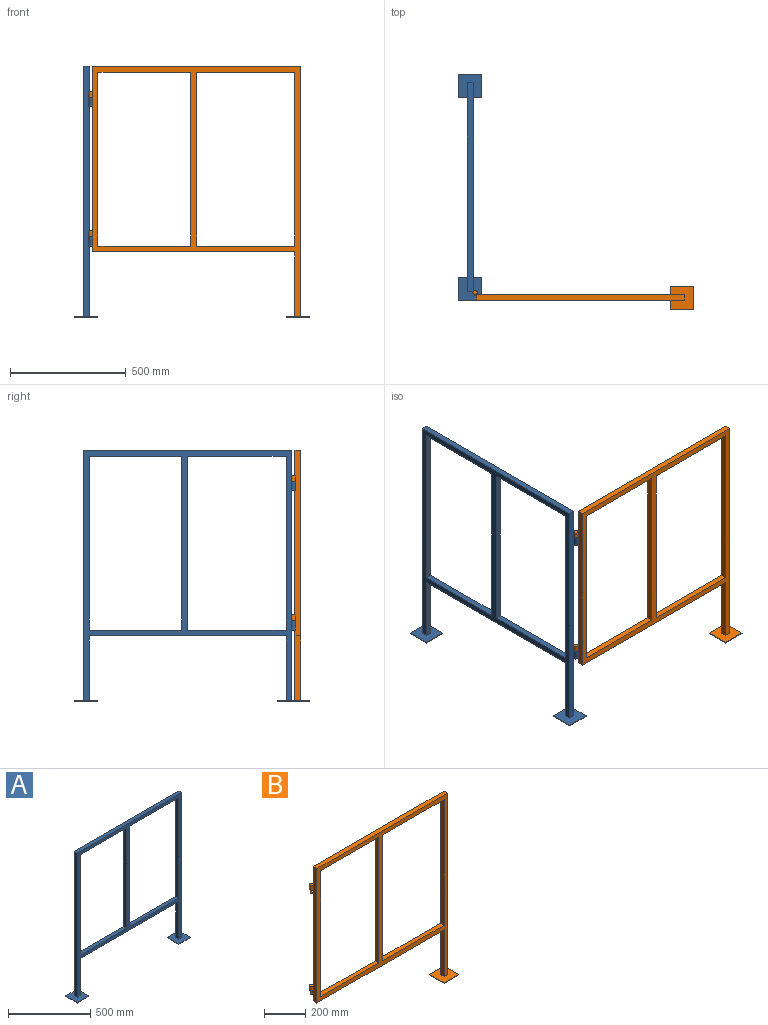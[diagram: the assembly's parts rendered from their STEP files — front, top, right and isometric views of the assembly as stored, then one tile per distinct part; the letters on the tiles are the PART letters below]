
ASSEMBLY  parts=2 mates=1
PART A: 38 faces, bbox 974.6x100x1083 mm
  f0: plane 1080x25.4mm, normal (-1,0,0), area 27432mm2, adj f13,f14,f15,f16
  f1: plane 280x25.4mm, normal (1,0,0), area 7112mm2, adj f2,f14,f15,f16
  f2: plane 849.2x25.4mm, normal (0,0,-1), area 21569.7mm2, adj f1,f3,f14,f15
  f3: plane 280x25.4mm, normal (-1,0,0), area 7112mm2, adj f2,f14,f15,f22
  f4: plane 1080x25.4mm, normal (1,0,0), area 27361.7mm2, adj f13,f14,f15,f22,f28,f29,f30,f33
  f5: plane 749.2x25.4mm, normal (1,0,0), area 19029.7mm2, adj f6,f11,f14,f15
  f6: plane 423.8x25.4mm, normal (0,0,-1), area 10764.5mm2, adj f5,f7,f14,f15
  f7: plane 749.2x25.4mm, normal (-1,0,0), area 19029.7mm2, adj f6,f11,f14,f15
  f8: plane 749.2x25.4mm, normal (1,0,0), area 19029.7mm2, adj f9,f12,f14,f15
  f9: plane 400x25.4mm, normal (0,0,-1), area 10160mm2, adj f8,f10,f14,f15
  f10: plane 749.2x25.4mm, normal (-1,0,0), area 19029.7mm2, adj f9,f12,f14,f15
  f11: plane 423.8x25.4mm, normal (0,0,1), area 10764.5mm2, adj f5,f7,f14,f15
  f12: plane 400x25.4mm, normal (0,0,1), area 10160mm2, adj f8,f10,f14,f15
  f13: plane 900x25.4mm, normal (0,0,1), area 22860mm2, adj f0,f4,f14,f15
  f14: plane 1080x900mm, normal (0,1,0), area 116921mm2, adj f0,f1,f2,f3,f4,f5,f6,f7
  f15: plane 1080x900mm, normal (0,-1,0), area 117033mm2, adj f0,f1,f2,f3,f4,f5,f6,f7
  f16: plane 100x100mm, normal (0,0,1), area 9354.8mm2, adj f0,f1,f14,f15,f17,f18,f19,f20
  f17: plane 100x3mm, normal (0,-1,0), area 300mm2, adj f16,f18,f20,f21
  f18: plane 100x3mm, normal (-1,0,0), area 300mm2, adj f16,f17,f19,f21
  f19: plane 100x3mm, normal (0,1,0), area 300mm2, adj f16,f18,f20,f21
  f20: plane 100x3mm, normal (1,0,0), area 300mm2, adj f16,f17,f19,f21
  f21: plane 100x100mm, normal (0,0,-1), area 10000mm2, adj f17,f18,f19,f20
  f22: plane 100x100mm, normal (0,0,1), area 9354.8mm2, adj f3,f4,f14,f15,f23,f24,f25,f26
  f23: plane 100x3mm, normal (0,-1,0), area 300mm2, adj f22,f24,f26,f27
  f24: plane 100x3mm, normal (-1,0,0), area 300mm2, adj f22,f23,f25,f27
  f25: plane 100x3mm, normal (0,1,0), area 300mm2, adj f22,f24,f26,f27
  f26: plane 100x3mm, normal (1,0,0), area 300mm2, adj f22,f23,f25,f27
  f27: plane 100x100mm, normal (0,0,-1), area 10000mm2, adj f23,f24,f25,f26
  f28: cylinder r=10mm len=40mm, axis (0,0,-1), area 2447.1mm2, adj f4,f14,f29,f30
  f29: plane 20x20mm, normal (0,0,1), area 235mm2, adj f4,f14,f28,f31
  f30: plane 20x20mm, normal (0,0,-1), area 313.5mm2, adj f4,f14,f28
  f31: cylinder r=5mm len=25mm, axis (0,0,1), area 785.4mm2, adj f29,f32
  f32: plane 10x10mm, normal (0,0,1), area 78.5mm2, adj f31
  f33: cylinder r=10mm len=40mm, axis (0,0,-1), area 2447.1mm2, adj f4,f14,f34,f35
  f34: plane 20x20mm, normal (0,0,1), area 235mm2, adj f4,f14,f33,f36
  f35: plane 20x20mm, normal (0,0,-1), area 313.5mm2, adj f4,f14,f33
  f36: cylinder r=5mm len=25mm, axis (0,0,1), area 785.4mm2, adj f34,f37
  f37: plane 10x10mm, normal (0,0,1), area 78.5mm2, adj f36
PART B: 31 faces, bbox 951.9x100x1083 mm
  f0: plane 400x25.4mm, normal (0,0,-1), area 10160mm2, adj f1,f12,f13,f14
  f1: plane 749.2x25.4mm, normal (-1,0,0), area 19029.7mm2, adj f0,f2,f13,f14
  f2: plane 400x25.4mm, normal (0,0,1), area 10160mm2, adj f1,f12,f13,f14
  f3: plane 1080x25.4mm, normal (1,0,0), area 27432mm2, adj f4,f13,f14,f20
  f4: plane 900x25.4mm, normal (0,0,1), area 22860mm2, adj f3,f5,f13,f14
  f5: plane 800x25.4mm, normal (-1,0,0), area 20276mm2, adj f4,f6,f13,f14,f21,f22,f23,f26
  f6: plane 874.6x25.4mm, normal (0,0,-1), area 22214.8mm2, adj f5,f7,f13,f14
  f7: plane 280x25.4mm, normal (-1,0,0), area 7112mm2, adj f6,f13,f14,f20
  f8: plane 749.2x25.4mm, normal (1,0,0), area 19029.7mm2, adj f9,f11,f13,f14
  f9: plane 423.8x25.4mm, normal (0,0,-1), area 10764.5mm2, adj f8,f10,f13,f14
  f10: plane 749.2x25.4mm, normal (-1,0,0), area 19029.7mm2, adj f9,f11,f13,f14
  f11: plane 423.8x25.4mm, normal (0,0,1), area 10764.5mm2, adj f8,f10,f13,f14
  f12: plane 749.2x25.4mm, normal (1,0,0), area 19029.7mm2, adj f0,f2,f13,f14
  f13: plane 1080x900mm, normal (0,1,0), area 109851mm2, adj f0,f1,f2,f3,f4,f5,f6,f7
  f14: plane 1080x900mm, normal (0,-1,0), area 109921mm2, adj f0,f1,f2,f3,f4,f5,f6,f7
  f15: plane 100x3mm, normal (0,-1,0), area 300mm2, adj f16,f18,f19,f20
  f16: plane 100x3mm, normal (-1,0,0), area 300mm2, adj f15,f17,f19,f20
  f17: plane 100x3mm, normal (0,1,0), area 300mm2, adj f16,f18,f19,f20
  f18: plane 100x3mm, normal (1,0,0), area 300mm2, adj f15,f17,f19,f20
  f19: plane 100x100mm, normal (0,0,-1), area 10000mm2, adj f15,f16,f17,f18
  f20: plane 100x100mm, normal (0,0,1), area 9354.8mm2, adj f3,f7,f13,f14,f15,f16,f17,f18
  f21: cylinder r=10mm len=25mm, axis (0,0,-1), area 1529.4mm2, adj f5,f13,f22,f23
  f22: plane 20x20mm, normal (0,0,1), area 313.5mm2, adj f5,f13,f21
  f23: plane 20x20mm, normal (0,0,-1), area 235mm2, adj f5,f13,f21,f24
  f24: cylinder r=5mm len=25mm, axis (0,0,1), area 785.4mm2, adj f23,f25
  f25: plane 10x10mm, normal (0,0,-1), area 78.5mm2, adj f24
  f26: cylinder r=10mm len=25mm, axis (0,0,-1), area 1529.4mm2, adj f5,f13,f27,f28
  f27: plane 20x20mm, normal (0,0,1), area 313.5mm2, adj f5,f13,f26
  f28: plane 20x20mm, normal (0,0,-1), area 235mm2, adj f5,f13,f26,f29
  f29: cylinder r=5mm len=25mm, axis (0,0,1), area 785.4mm2, adj f28,f30
  f30: plane 10x10mm, normal (0,0,-1), area 78.5mm2, adj f29
PLACE A rot(axis=(0,0,-1),90deg) t=(-327.04,634.54,-143.43)mm
PLACE B rot(axis=(0.9,-0.42,0.1),0deg) t=(-975.52,110.06,-143.43)mm
MATE revolute B.f21 <-> A.f28  axis (0,0,-1) through (-293.64,143.46,-103.43)mm
